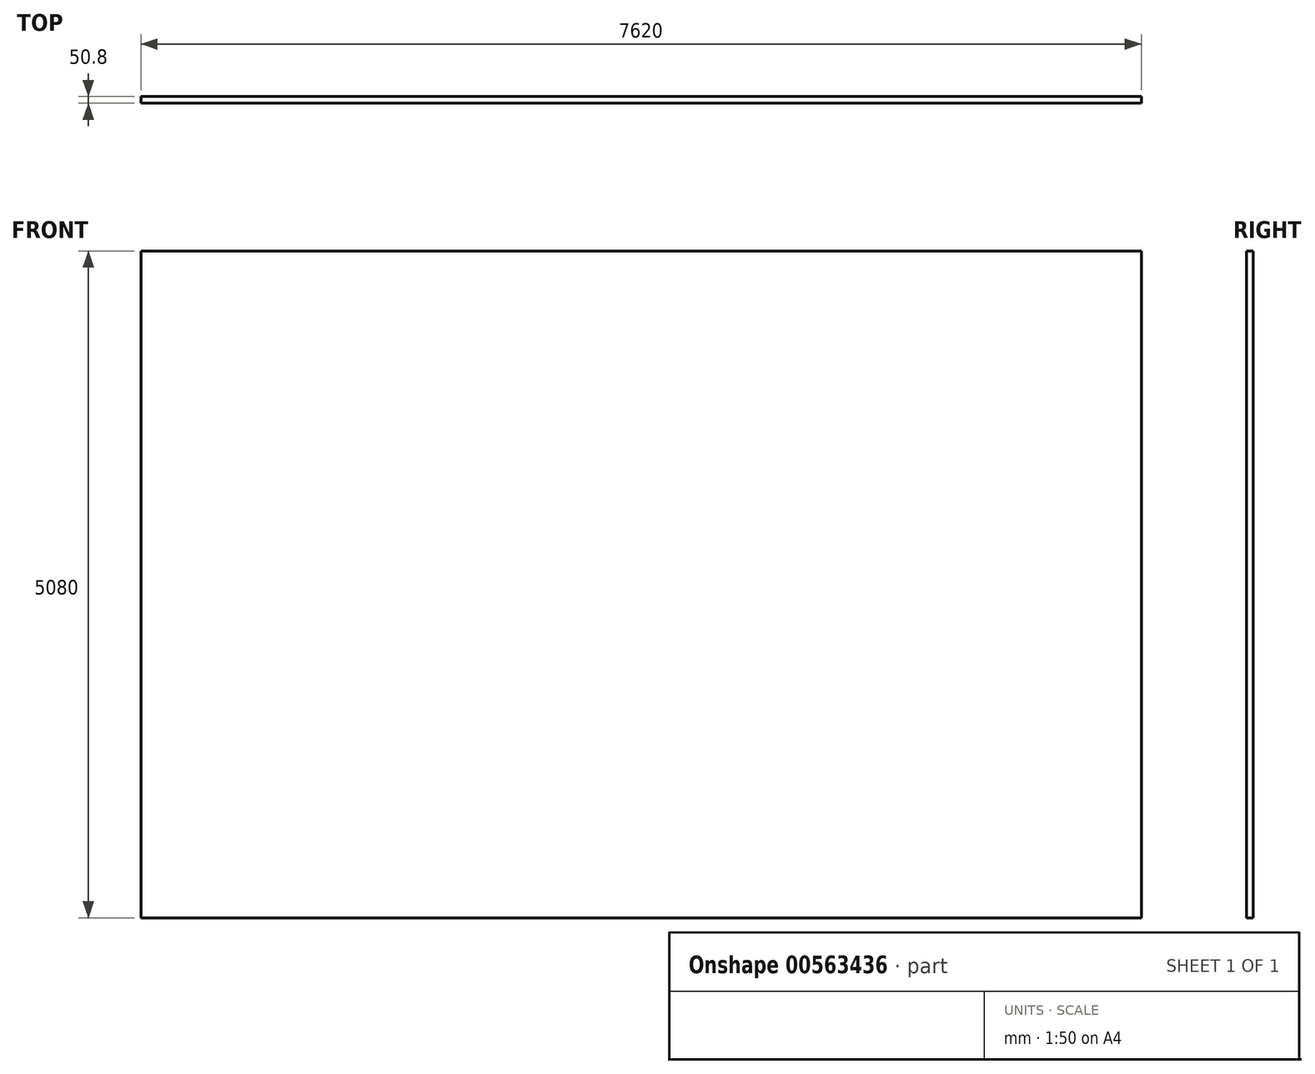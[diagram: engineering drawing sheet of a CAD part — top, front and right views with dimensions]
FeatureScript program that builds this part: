
annotation { "Feature Type Name" : "Feature", "Feature Type Description" : "" }
export const myFeature = defineFeature(function(context is Context, id is Id, definition is map)
    precondition{}
    {
        {
            var Q0;
            Q0=qCreatedBy(makeId("Front.planeOp"),FACE);
            var sketch = newSketch(context, id + "F0", { "sketchPlane" : qUnion([Q0])});
            skLineSegment(sketch, "E0.bottom", {"start": v(-3810, -2540) * mm, "end": v(3810, -2540) * mm});
            skLineSegment(sketch, "E0.top", {"start": v(-3810, 2540) * mm, "end": v(3810, 2540) * mm});
            skLineSegment(sketch, "E0.left", {"start": v(-3810, -2540) * mm, "end": v(-3810, 2540) * mm});
            skLineSegment(sketch, "E0.right", {"start": v(3810, -2540) * mm, "end": v(3810, 2540) * mm});
            skPoint(sketch, "E0.middle", {"position": v(0, 0) * mm});
            skSolve(sketch);
        }
        {
            var Q0;
            Q0 = qSketchRegion(id + "F0", true);
            extrude(context, id + "F1", {"entities" : qUnion([Q0]), "depth" : 50.8 * mm, "offsetDistance" : 25.4 * mm});
        }
    });
